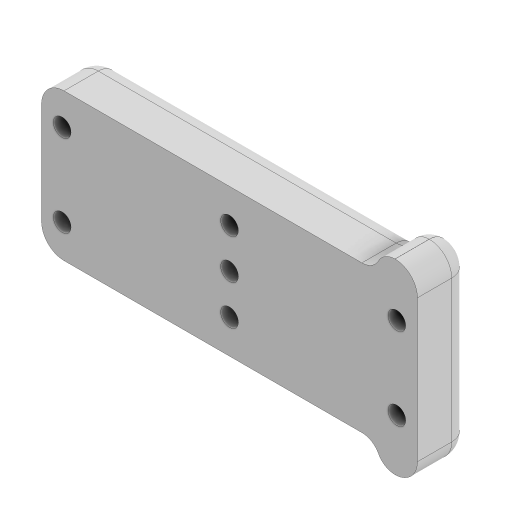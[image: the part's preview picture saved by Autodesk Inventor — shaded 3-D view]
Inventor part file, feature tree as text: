
AUTODESK INVENTOR PART (.ipt)
format: ipt  version: 2024 (Build 280153000, 153)  size: 326,656 bytes
history: native  units: in
note: dims shown in document units (in); Inventor stores cm internally (conversion verified against a paired STEP export)
features: projected_geometry x15, extrude x9, sketch x9, fillet x5
ambient origin geometry x8: Origin, YZ Plane, XZ Plane, XY Plane, X Axis, Y Axis, Z Axis, Center Point
bodies: Solid1 (feature_tree)
feature tree (38):
  extrude  "Extrusion1"  Depth=0.15in TaperAngle=0.0deg
  extrude  "Extrusion2"  Depth=0.354in TaperAngle=0.0deg
  extrude  "Extrusion3"  Depth=0.177in
  extrude  "Extrusion4"  Depth=0.1575in
  extrude  "Extrusion7"  Depth=0.125in TaperAngle=0.0deg
  fillet  "Fillet5"  Radius=0.125in
  extrude  "Extrusion9"  Depth=0.1476in TaperAngle=0.0deg
  extrude  "Extrusion10"  Depth=0.125in
  fillet  "Fillet17"  Radius=0.2972in
  fillet  "Fillet18"  Radius=0.15in
  fillet  "Fillet19"  Radius=0.125in
  extrude  "Extrusion11"  Depth=0.125in TaperAngle=0.0deg
  fillet  "Fillet23"  Radius=0.125in
  extrude  "Extrusion14"  TaperAngle=0.0deg  [1 undecoded]
  sketch  "Sketch1"  dims[d1=0.2in d2=0.15in d3=0.0in]
  sketch  "Sketch2"  dims[d4=0.0625in d5=0.0in d6=0.354in d7=0.0in]
  projected_geometry  "Projected Loop1"
  sketch  "Sketch3"  dims[d8=0.177in d9=0.177in]
  sketch  "Sketch4"  dims[d10=0.1575in d11=0.1575in]
  sketch  "Sketch7"  dims[d12=0.4in d13=0.0in d22=0.2476in d23=0.0in d24=0.125in]
  projected_geometry  "Projected Loop4"
  sketch  "Sketch9"  dims[d26=0.275in d27=0.275in d28=0.1181in d29=0.1181in d34=0.1476in d35=0.0in]
  sketch  "Sketch10"  dims[d36=0.3543in d37=0.0in d47=0.075in d48=0.2972in d49=0.15in d50=0.125in]
  projected_geometry  "Projected Loop5"
  projected_geometry  "Projected Loop6"
  projected_geometry  "Projected Loop7"
  projected_geometry  "Projected Loop8"
  projected_geometry  "Projected Loop9"
  projected_geometry  "Projected Loop10"
  projected_geometry  "Projected Loop11"
  projected_geometry  "Projected Loop12"
  projected_geometry  "Projected Loop13"
  projected_geometry  "Projected Loop14"
  projected_geometry  "Projected Loop15"
  projected_geometry  "Projected Loop16"
  sketch  "Sketch11"  dims[d51=0.125in d55=1.0in d56=0.0in d62=0.125in]
  projected_geometry  "Projected Loop17"
  sketch  "Sketch14"  dims[d63=1.0in d64=0.0in d53=0.0in d54=0.0in]
note: 1 required parameter value undecoded (feature->parameter linkage not recoverable at this tier; creation-order binding heuristic only, values carry confidence <= 0.55)
